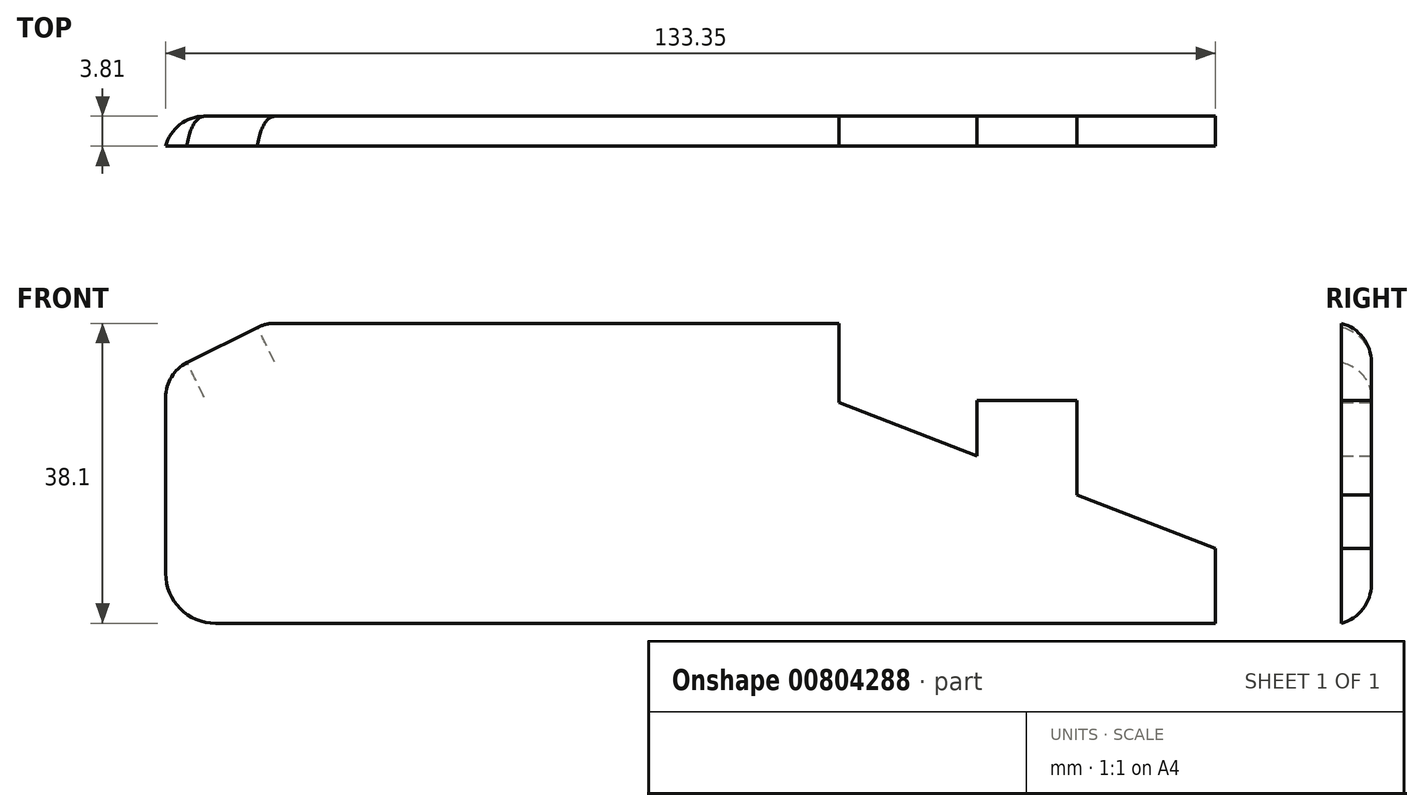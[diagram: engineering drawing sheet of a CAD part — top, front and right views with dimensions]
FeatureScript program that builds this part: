
annotation { "Feature Type Name" : "Feature", "Feature Type Description" : "" }
export const myFeature = defineFeature(function(context is Context, id is Id, definition is map)
    precondition{}
    {
        {
            var Q0;
            Q0=qCreatedBy(makeId("Front.planeOp"),FACE);
            var sketch = newSketch(context, id + "F0", { "sketchPlane" : qUnion([Q0])});
            skLineSegment(sketch, "E0", {"start": v(0, 0) * mm, "end": v(-101.6, 0) * mm});
            skLineSegment(sketch, "E1", {"start": v(-107.95, 6.35) * mm, "end": v(-107.95, 31.75) * mm});
            skLineSegment(sketch, "E2", {"start": v(-95.25, 38.1) * mm, "end": v(-47.62, 38.1) * mm});
            skLineSegment(sketch, "E3", {"start": v(-107.95, 31.75) * mm, "end": v(-95.25, 38.1) * mm});
            skPoint(sketch, "E4.visualSharp", {"position": v(-107.95, 0) * mm});
            skArc(sketch, "E4.filletArc", {"start": v(-107.95, 6.35) * mm, "mid": v(-106.1, 1.86) * mm, "end": v(-101.6, 0) * mm});
            skLineSegment(sketch, "E5", {"start": v(0, 0) * mm, "end": v(25.4, 0) * mm});
            skLineSegment(sketch, "E6", {"start": v(25.4, 9.52) * mm, "end": v(25.4, 0) * mm});
            skLineSegment(sketch, "E7", {"start": v(-47.62, 38.1) * mm, "end": v(-22.44, 38.1) * mm});
            skLineSegment(sketch, "E8", {"start": v(-22.44, 28.03) * mm, "end": v(-22.44, 38.1) * mm});
            skLineSegment(sketch, "E9", {"start": v(-22.44, 28.03) * mm, "end": v(-4.87, 21.23) * mm});
            skLineSegment(sketch, "E10", {"start": v(-4.87, 28.3) * mm, "end": v(-4.87, 21.23) * mm});
            skLineSegment(sketch, "E11", {"start": v(7.83, 28.3) * mm, "end": v(7.83, 16.32) * mm});
            skLineSegment(sketch, "E12", {"start": v(-4.87, 28.3) * mm, "end": v(7.83, 28.3) * mm});
            skLineSegment(sketch, "E13.trimOffspring", {"start": v(7.83, 16.32) * mm, "end": v(25.4, 9.53) * mm});
            skSolve(sketch);
        }
        {
            var Q0;
            Q0=makeQuery(id+"F0.imprint","IMPRINT",FACE,{"disambiguationData":[TD([[makeQuery(id+"F0.imprint","IMPRINT",EDGE,{"derivedFrom":sQuery(id+"F0.wireOp",EDGE,"E0")}),-1.0]])]});
            var Q1;
            {var subQ0=sQuery(id+"F0.wireOp",EDGE,"UkxAD6a5-Vf1N-LSM3-fqia-8ZDhw41AiqvJ");Q1=makeQuery(id+"F0.imprint","IMPRINT",FACE,{"disambiguationData":[TD([[makeQuery(id+"F0.imprint","IMPRINT",EDGE,{"derivedFrom":subQ0}),-1.0]])]});}
            extrude(context, id + "F1", {"entities" : qUnion([Q0, Q1]), "depth" : 3.8 * mm, "offsetDistance" : 25.4 * mm});
        }
        {
            var Q0;
            Q0=makeQuery(id+"F1.opExtrude","CAP_EDGE",EDGE,{"disambiguationData":[OSD([sQuery(id+"F0.wireOp",EDGE,"E0"),sQuery(id+"F0.wireOp",EDGE,"E5")])],"isStart":true});
            var Q1;
            Q1=makeQuery(id+"F1.opExtrude","CAP_EDGE",EDGE,{"disambiguationData":[OSD([sQuery(id+"F0.wireOp",EDGE,"E4.filletArc")])],"isStart":true});
            var Q2;
            Q2=makeQuery(id+"F1.opExtrude","CAP_EDGE",EDGE,{"disambiguationData":[OSD([sQuery(id+"F0.wireOp",EDGE,"E1")])],"isStart":true});
            var Q3;
            Q3=makeQuery(id+"F1.opExtrude","CAP_EDGE",EDGE,{"disambiguationData":[OSD([sQuery(id+"F0.wireOp",EDGE,"E3")])],"isStart":true});
            var Q4;
            Q4=makeQuery(id+"F1.opExtrude","CAP_EDGE",EDGE,{"disambiguationData":[OSD([sQuery(id+"F0.wireOp",EDGE,"E2")])],"isStart":true});
            fillet(context, id + "F2", {"entities" : qUnion([Q0, Q1, Q2, Q3, Q4]), "radius" : 5.08 * mm, "tangentPropagation" : true, "allowEdgeOverflow" : false});
        }
        {
            var Q0;
            Q0=makeQuery(id+"F2.opFillet","BLEND_EDGE",EDGE,{"blendedFrom":[makeQuery(id+"F1.opExtrude","CAP_EDGE",EDGE,{"disambiguationData":[OSD([sQuery(id+"F0.wireOp",EDGE,"E1")])],"isStart":true}),makeQuery(id+"F1.opExtrude","CAP_EDGE",EDGE,{"disambiguationData":[OSD([sQuery(id+"F0.wireOp",EDGE,"E3")])],"isStart":true})],"blendedInto":[]});
            var Q1;
            Q1=makeQuery(id+"F2.opFillet","BLEND_EDGE",EDGE,{"blendedFrom":[makeQuery(id+"F1.opExtrude","CAP_EDGE",EDGE,{"disambiguationData":[OSD([sQuery(id+"F0.wireOp",EDGE,"E2"),sQuery(id+"F0.wireOp",EDGE,"E7")])],"isStart":true}),makeQuery(id+"F1.opExtrude","CAP_EDGE",EDGE,{"disambiguationData":[OSD([sQuery(id+"F0.wireOp",EDGE,"E3")])],"isStart":true})],"blendedInto":[]});
            fillet(context, id + "F3", {"entities" : qUnion([Q0, Q1]), "radius" : 5.08 * mm, "tangentPropagation" : true, "allowEdgeOverflow" : false});
        }
    });
